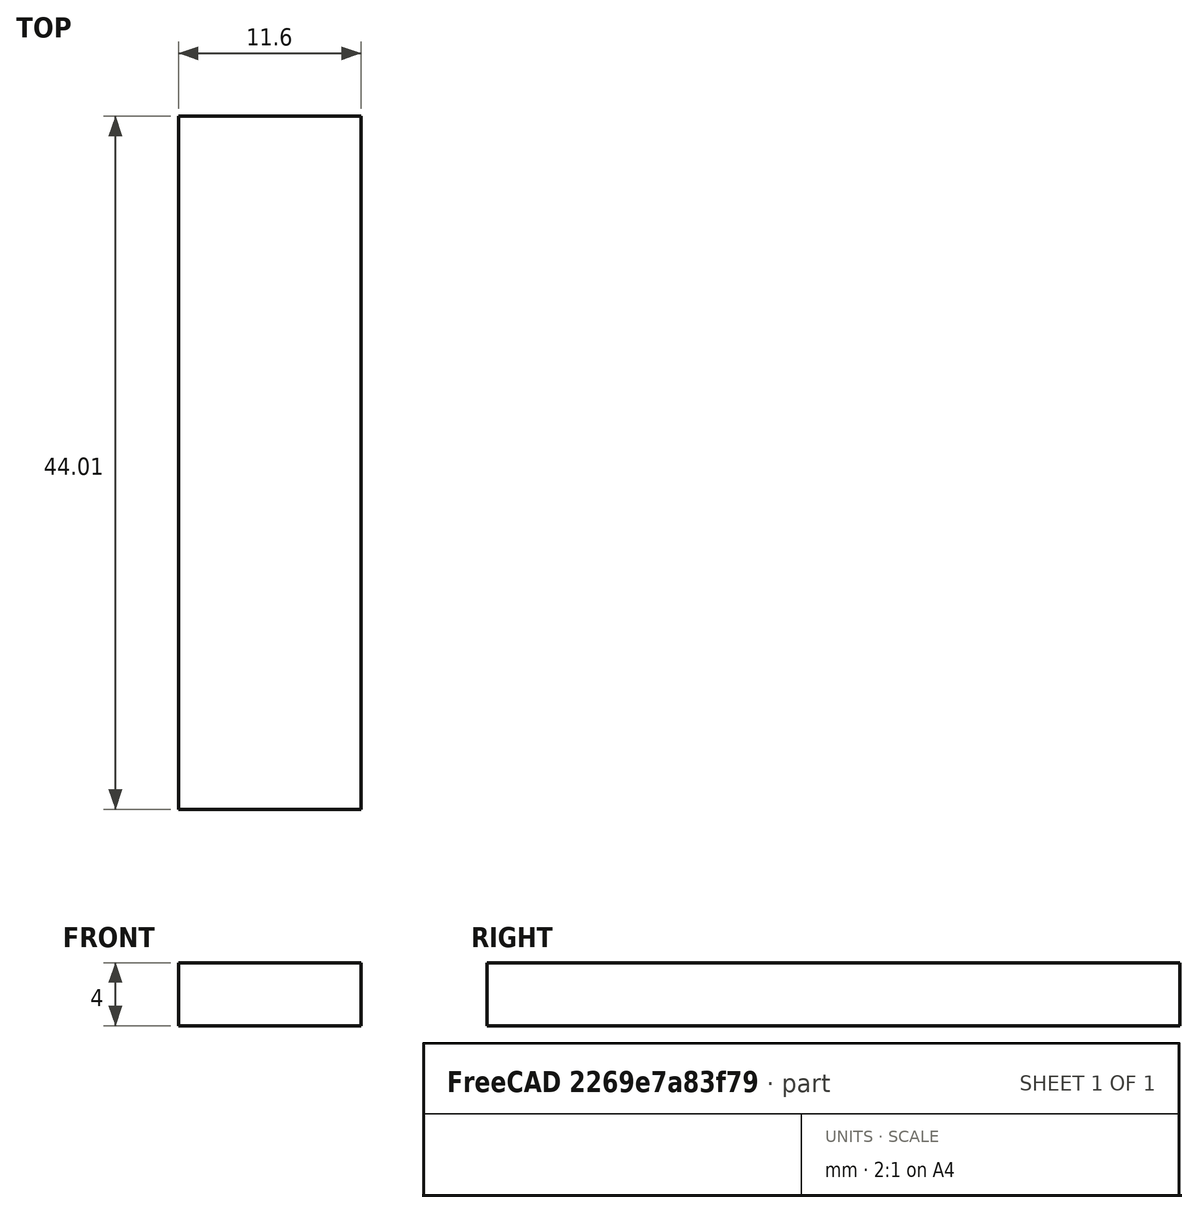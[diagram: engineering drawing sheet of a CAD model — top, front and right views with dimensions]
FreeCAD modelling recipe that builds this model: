
FCSTD DOCUMENT  (FreeCAD 0.21R33771 (Git))
Label: battery mk2
License: All rights reserved
LicenseURL: https://en.wikipedia.org/wiki/All_rights_reserved
objects: Mesh::Feature×2, Part::Feature×2, Sketcher::SketchObject×1, PartDesign::Pad×1, PartDesign::Body×1
note: 6 computed .brp shape members not serialized (recipe doc carries the construction recipe); baked Part::Feature solids carry a one-line shape summary decoded from their .brp

FEATURE [Mesh::Feature] __Batterie_2_0___Copy  label="2_Batterie_2.0 - Copy"
  Placement = pos=(89.2,0,0) rot=(0,0,1;0rad)
FEATURE [Mesh::Feature] __Batterie_2_0  label="2_Batterie_2.0"
FEATURE [Sketcher::SketchObject] Sketch
  FullyConstrained = false
  MapMode = 5
  Placement = pos=(0,0,0) rot=(0.57735,0.57735,0.57735;2.0944rad)
  Support = -> [YZ_Plane001]
  sketch-geometry (4):
    g0: LineSegment StartX=0 StartY=19.9937 StartZ=0 EndX=44.01 EndY=19.9937 EndZ=0
    g1: LineSegment StartX=44.01 StartY=19.9937 StartZ=0 EndX=44.01 EndY=15.9856 EndZ=0
    g2: LineSegment StartX=44.01 StartY=15.9856 StartZ=0 EndX=0 EndY=15.9856 EndZ=0
    g3: LineSegment StartX=0 StartY=15.9856 StartZ=0 EndX=0 EndY=19.9937 EndZ=0
  constraints (10):
    c: Coincident(g0,g1)
    c: Coincident(g1,g2)
    c: Coincident(g2,g3)
    c: Coincident(g3,g0)
    c: Horizontal(g0)
    c: Horizontal(g2)
    c: Vertical(g1)
    c: Vertical(g3)
    c: PointOnObject(g0,g-2)
    c: DistanceX(g0,g0) = 44.01
FEATURE [PartDesign::Pad] Pad
  Direction = (1,-2e-16,3e-16)
  Length = 11.6
  Length2 = 10
  Placement = pos=(0,0,0) rot=(1,1,1;2.0944rad)
  Profile = -> Sketch
  ReferenceAxis = -> Sketch [N_Axis]
  Type = 0
FEATURE [PartDesign::Body] Body001
  Group = -> [Sketch,Pad]
  Origin = -> Origin001
  Placement = pos=(79.5,0,0) rot=(0,0,1;0rad)
  Tip = -> Pad
FEATURE [Part::Feature] __Batterie_2_0___Copy001
  shape: bbox 81.4 x 44 x 20 mm, 17624 faces, 0 solids (baked)
FEATURE [Part::Feature] __Batterie_2_001
  shape: bbox 81.4 x 44 x 20 mm, 17624 faces, 0 solids (baked)
